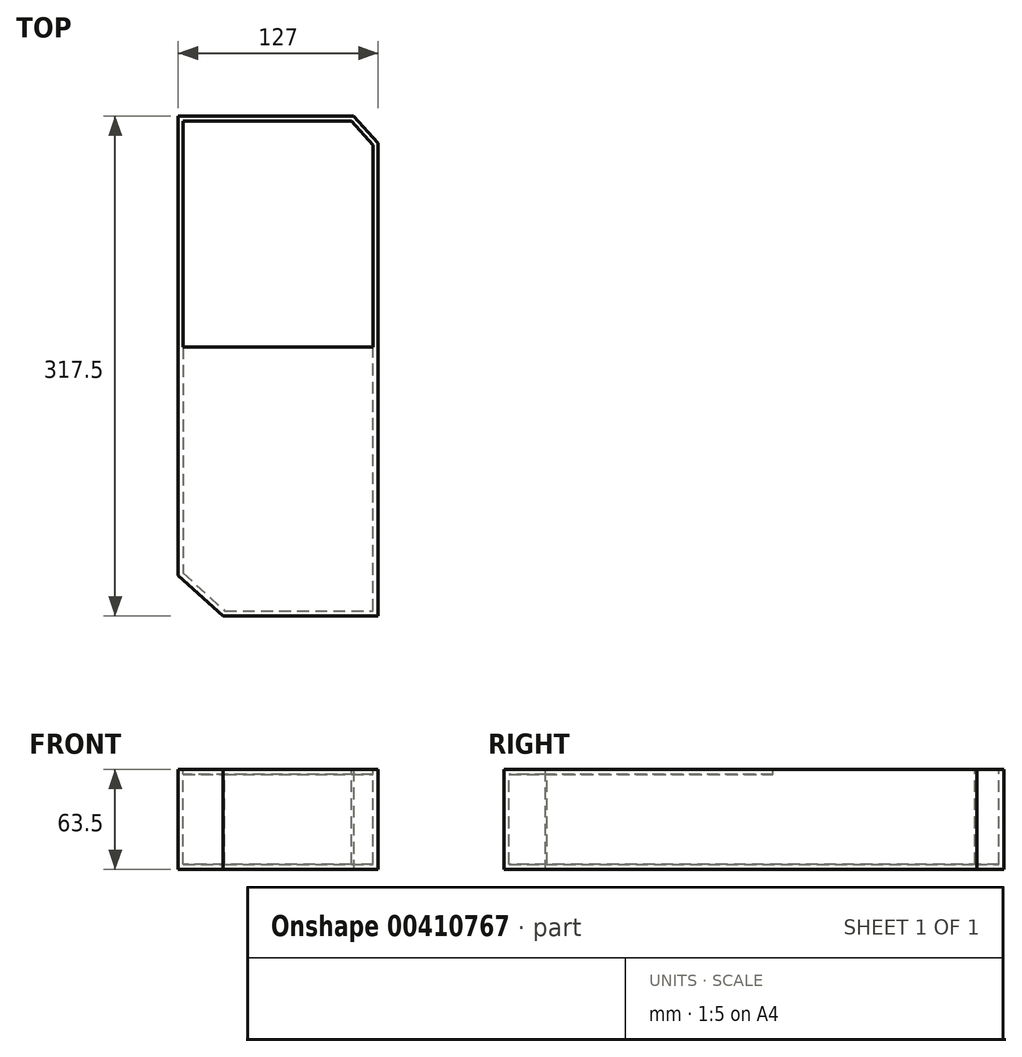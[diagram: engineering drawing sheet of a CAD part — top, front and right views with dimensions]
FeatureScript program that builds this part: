
annotation { "Feature Type Name" : "Feature", "Feature Type Description" : "" }
export const myFeature = defineFeature(function(context is Context, id is Id, definition is map)
    precondition{}
    {
        {
            var Q0;
            Q0=qCreatedBy(makeId("Top.planeOp"),FACE);
            var sketch = newSketch(context, id + "F0", { "sketchPlane" : qUnion([Q0])});
            skLineSegment(sketch, "E0.bottom", {"start": v(47.93, 158.75) * mm, "end": v(-63.5, 158.75) * mm});
            skLineSegment(sketch, "E0.top", {"start": v(63.5, -158.75) * mm, "end": v(-35.14, -158.75) * mm});
            skLineSegment(sketch, "E0.left", {"start": v(63.5, 141.65) * mm, "end": v(63.5, -158.75) * mm});
            skLineSegment(sketch, "E0.right", {"start": v(-63.5, 158.75) * mm, "end": v(-63.5, -132.91) * mm});
            skPoint(sketch, "E0.middle", {"position": v(0, 0) * mm});
            skLineSegment(sketch, "E1", {"start": v(47.93, 158.75) * mm, "end": v(63.77, 141.36) * mm});
            skPoint(sketch, "E2.orphan", {"position": v(63.5, 158.75) * mm});
            skLineSegment(sketch, "E3", {"start": v(-63.5, -132.91) * mm, "end": v(-35.14, -158.75) * mm});
            skPoint(sketch, "E4.orphan", {"position": v(-63.5, -158.75) * mm});
            skSolve(sketch);
        }
        {
            var Q0;
            Q0=makeQuery(id+"F0.imprint","IMPRINT",FACE,{"disambiguationData":[TD([[makeQuery(id+"F0.imprint","IMPRINT",EDGE,{"derivedFrom":sQuery(id+"F0.wireOp",EDGE,"E0.bottom")}),1.0]])]});
            extrude(context, id + "F1", {"entities" : qUnion([Q0]), "depth" : 63.5 * mm, "offsetDistance" : 25.4 * mm, "symmetric" : true});
        }
        {
            var Q0;
            Q0=makeQuery(id+"F1.opExtrude","CAP_FACE",FACE,{"disambiguationData":[OSD([sQuery(id+"F0.wireOp",EDGE,"E0.bottom"),sQuery(id+"F0.wireOp",EDGE,"E0.top"),sQuery(id+"F0.wireOp",EDGE,"E0.left"),sQuery(id+"F0.wireOp",EDGE,"E0.right"),sQuery(id+"F0.wireOp",EDGE,"E1"),sQuery(id+"F0.wireOp",EDGE,"E3")])],"isStart":false});
            var sketch = newSketch(context, id + "F2", { "sketchPlane" : qUnion([Q0])});
            skLineSegment(sketch, "E5.0", {"start": v(-33.91, -155.58) * mm, "end": v(60.33, -155.58) * mm});
            skLineSegment(sketch, "E5.1", {"start": v(60.33, 140.42) * mm, "end": v(46.52, 155.58) * mm});
            skLineSegment(sketch, "E5.2", {"start": v(46.52, 155.58) * mm, "end": v(-60.32, 155.58) * mm});
            skLineSegment(sketch, "E5.3", {"start": v(60.33, -155.58) * mm, "end": v(60.33, 140.42) * mm});
            skLineSegment(sketch, "E5.4", {"start": v(-60.32, 155.58) * mm, "end": v(-60.33, -131.51) * mm});
            skLineSegment(sketch, "E5.5", {"start": v(-60.33, -131.51) * mm, "end": v(-33.91, -155.58) * mm});
            skSolve(sketch);
        }
        {
            var Q0;
            Q0=makeQuery(id+"F2.imprint","IMPRINT",FACE,{"disambiguationData":[TD([[makeQuery(id+"F2.imprint","IMPRINT",EDGE,{"derivedFrom":sQuery(id+"F2.wireOp",EDGE,"E5.0")}),1.0]])]});
            extrude(context, id + "F3", {"entities" : qUnion([Q0]), "operationType" : NewBodyOperationType.REMOVE, "oppositeDirection" : true, "depth" : 60.32 * mm, "offsetDistance" : 25.4 * mm});
        }
        {
            var Q0;
            Q0=makeQuery(id+"F1.opExtrude","CAP_FACE",FACE,{"disambiguationData":[OSD([sQuery(id+"F0.wireOp",EDGE,"E0.bottom"),sQuery(id+"F0.wireOp",EDGE,"E0.top"),sQuery(id+"F0.wireOp",EDGE,"E0.left"),sQuery(id+"F0.wireOp",EDGE,"E0.right"),sQuery(id+"F0.wireOp",EDGE,"E1"),sQuery(id+"F0.wireOp",EDGE,"E3")])],"isStart":false});
            var sketch = newSketch(context, id + "F4", { "sketchPlane" : qUnion([Q0])});
            skLineSegment(sketch, "E6", {"start": v(-60.33, 12.03) * mm, "end": v(-60.33, -131.51) * mm});
            skLineSegment(sketch, "E7", {"start": v(-60.33, -131.51) * mm, "end": v(-33.91, -155.58) * mm});
            skLineSegment(sketch, "E8", {"start": v(-33.91, -155.58) * mm, "end": v(60.33, -155.58) * mm});
            skLineSegment(sketch, "E9", {"start": v(60.33, -155.58) * mm, "end": v(60.33, 12.03) * mm});
            skLineSegment(sketch, "E10", {"start": v(60.33, 12.03) * mm, "end": v(-60.33, 12.03) * mm});
            skSolve(sketch);
        }
        {
            var Q0;
            Q0=makeQuery(id+"F4.imprint","IMPRINT",FACE,{"disambiguationData":[TD([[makeQuery(id+"F4.imprint","IMPRINT",EDGE,{"derivedFrom":sQuery(id+"F4.wireOp",EDGE,"E6")}),1.0]])]});
            extrude(context, id + "F5", {"entities" : qUnion([Q0]), "operationType" : NewBodyOperationType.ADD, "oppositeDirection" : true, "depth" : 3.17 * mm, "offsetDistance" : 25.4 * mm});
        }
    });
